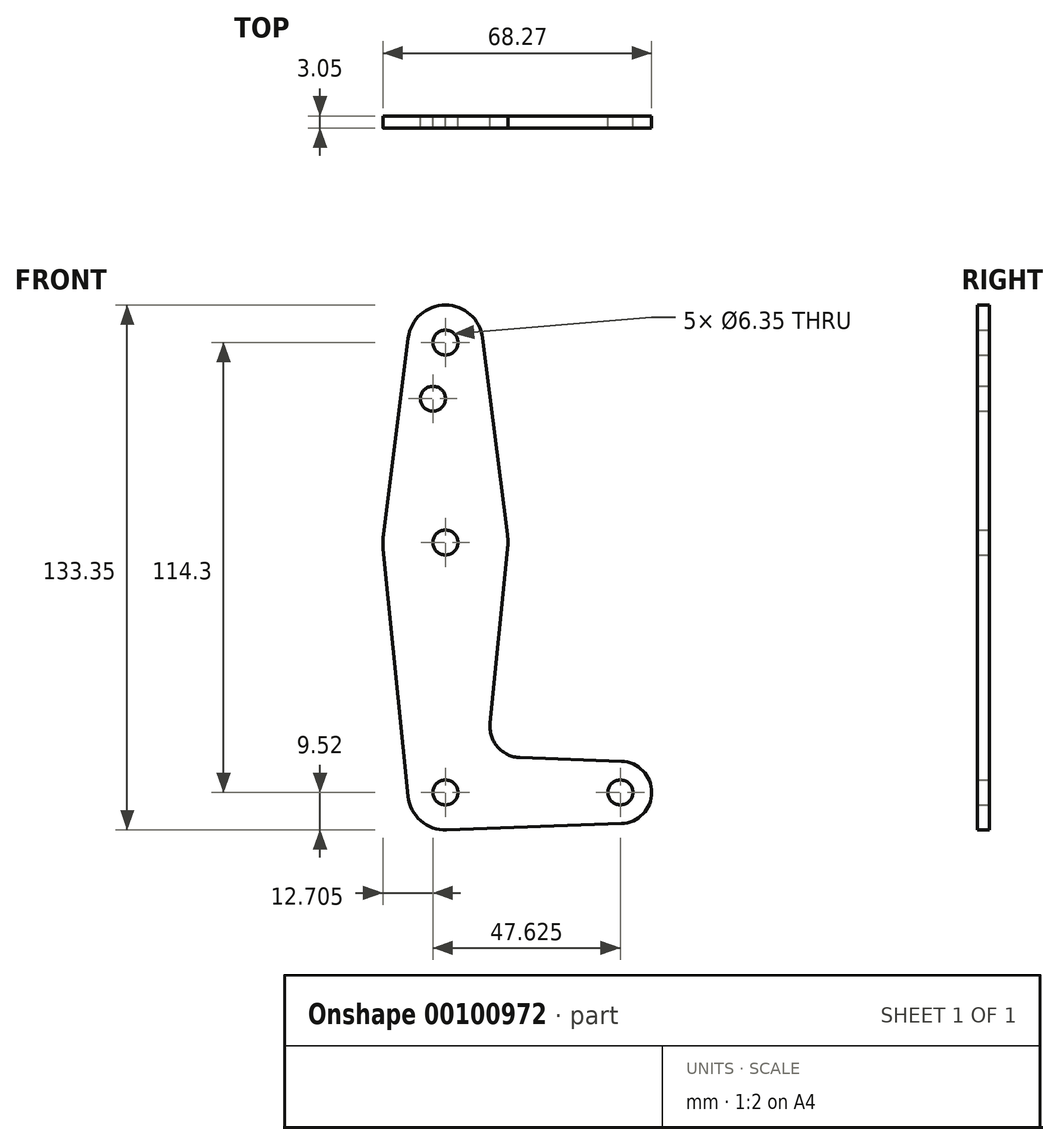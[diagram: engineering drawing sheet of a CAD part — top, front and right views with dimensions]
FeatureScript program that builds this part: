
annotation { "Feature Type Name" : "Feature", "Feature Type Description" : "" }
export const myFeature = defineFeature(function(context is Context, id is Id, definition is map)
    precondition{}
    {
        {
            var Q0;
            Q0=qCreatedBy(makeId("Front.planeOp"),FACE);
            var sketch = newSketch(context, id + "F0", { "sketchPlane" : qUnion([Q0])});
            skCircle(sketch, "E0", {"center": v(0, 0) * mm, "radius": 9.53 * mm});
            skCircle(sketch, "E1", {"center": v(44.45, 0) * mm, "radius": 7.94 * mm});
            skCircle(sketch, "E2", {"center": v(0, 63.5) * mm, "radius": 15.88 * mm});
            skCircle(sketch, "E3", {"center": v(0, 114.3) * mm, "radius": 9.53 * mm});
            skLineSegment(sketch, "E4", {"start": v(0, 114.3) * mm, "end": v(0, 63.5) * mm, "construction": true});
            skLineSegment(sketch, "E5", {"start": v(0, 63.5) * mm, "end": v(0, 0) * mm, "construction": true});
            skLineSegment(sketch, "E6", {"start": v(0, 0) * mm, "end": v(44.45, 0) * mm, "construction": true});
            skLineSegment(sketch, "E7", {"start": v(-9.45, 115.5) * mm, "end": v(-15.75, 65.48) * mm});
            skLineSegment(sketch, "E8", {"start": v(9.45, 115.5) * mm, "end": v(15.75, 65.48) * mm});
            skLineSegment(sketch, "E9", {"start": v(15.8, 61.91) * mm, "end": v(11.34, 17.6) * mm});
            skLineSegment(sketch, "E10", {"start": v(18.97, 8.85) * mm, "end": v(44.73, 7.93) * mm});
            skLineSegment(sketch, "E11", {"start": v(-15.8, 61.91) * mm, "end": v(-9.48, -0.95) * mm});
            skLineSegment(sketch, "E12", {"start": v(44.73, -7.93) * mm, "end": v(0.34, -9.52) * mm});
            skCircle(sketch, "E13", {"center": v(0, 114.3) * mm, "radius": 3.18 * mm});
            skCircle(sketch, "E14", {"center": v(-3.18, 100.03) * mm, "radius": 3.18 * mm});
            skCircle(sketch, "E15", {"center": v(0, 63.5) * mm, "radius": 3.18 * mm});
            skCircle(sketch, "E16", {"center": v(0, 0) * mm, "radius": 3.18 * mm});
            skCircle(sketch, "E17", {"center": v(44.45, 0) * mm, "radius": 3.18 * mm});
            skArc(sketch, "E18.filletArc", {"start": v(11.34, 17.6) * mm, "mid": v(13.26, 11.57) * mm, "end": v(18.97, 8.85) * mm});
            skSolve(sketch);
        }
        {
            var Q0;
            Q0 = qSketchRegion(id + "F0", true);
            extrude(context, id + "F1", {"entities" : qUnion([Q0]), "depth" : 3.05 * mm});
        }
    });
